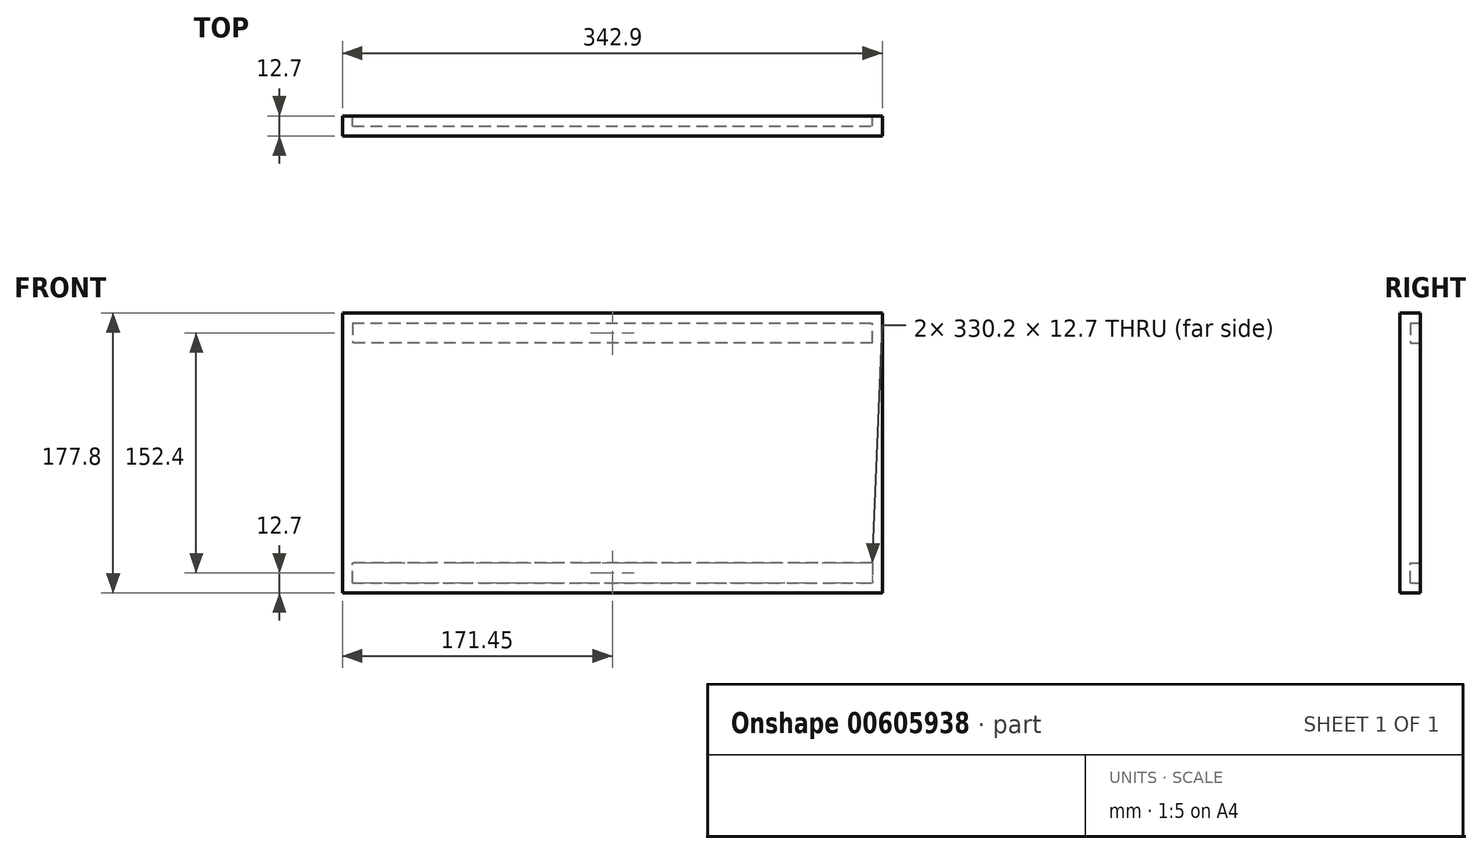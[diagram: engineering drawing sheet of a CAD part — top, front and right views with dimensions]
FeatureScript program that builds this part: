
annotation { "Feature Type Name" : "Feature", "Feature Type Description" : "" }
export const myFeature = defineFeature(function(context is Context, id is Id, definition is map)
    precondition{}
    {
        {
            var Q0;
            Q0=qCreatedBy(makeId("Front.planeOp"),FACE);
            var sketch = newSketch(context, id + "F0", { "sketchPlane" : qUnion([Q0])});
            skLineSegment(sketch, "E0.bottom", {"start": v(0, 0) * mm, "end": v(342.9, 0) * mm});
            skLineSegment(sketch, "E0.top", {"start": v(0, 177.8) * mm, "end": v(342.9, 177.8) * mm});
            skLineSegment(sketch, "E0.left", {"start": v(0, 0) * mm, "end": v(0, 177.8) * mm});
            skLineSegment(sketch, "E0.right", {"start": v(342.9, 0) * mm, "end": v(342.9, 177.8) * mm});
            skSolve(sketch);
        }
        {
            var Q0;
            Q0=makeQuery(id+"F0.imprint","IMPRINT",FACE,{"disambiguationData":[TD([[makeQuery(id+"F0.imprint","IMPRINT",EDGE,{"derivedFrom":sQuery(id+"F0.wireOp",EDGE,"E0.bottom")}),1.0]])]});
            extrude(context, id + "F1", {"entities" : qUnion([Q0]), "depth" : 12.7 * mm, "offsetDistance" : 25.4 * mm});
        }
        {
            var Q0;
            Q0=makeQuery(id+"F1.opExtrude","CAP_FACE",FACE,{"disambiguationData":[OSD([sQuery(id+"F0.wireOp",EDGE,"E0.bottom"),sQuery(id+"F0.wireOp",EDGE,"E0.top"),sQuery(id+"F0.wireOp",EDGE,"E0.left"),sQuery(id+"F0.wireOp",EDGE,"E0.right")])],"isStart":true});
            var sketch = newSketch(context, id + "F2", { "sketchPlane" : qUnion([Q0])});
            skLineSegment(sketch, "E1", {"start": v(-342.9, 0) * mm, "end": v(-342.9, 6.35) * mm});
            skLineSegment(sketch, "E2", {"start": v(-342.9, 6.35) * mm, "end": v(-342.9, 19.05) * mm});
            skLineSegment(sketch, "E3", {"start": v(-342.9, 19.05) * mm, "end": v(0, 19.05) * mm});
            skLineSegment(sketch, "E4", {"start": v(0, 19.05) * mm, "end": v(0, 6.35) * mm});
            skLineSegment(sketch, "E5", {"start": v(0, 6.35) * mm, "end": v(-342.9, 6.35) * mm});
            skLineSegment(sketch, "E6", {"start": v(-342.9, 19.05) * mm, "end": v(-336.55, 19.05) * mm});
            skLineSegment(sketch, "E7", {"start": v(-336.55, 19.05) * mm, "end": v(-336.55, 6.35) * mm});
            skLineSegment(sketch, "E8", {"start": v(-336.55, 6.35) * mm, "end": v(0, 6.35) * mm});
            skLineSegment(sketch, "E9", {"start": v(0, 6.35) * mm, "end": v(-6.35, 6.35) * mm});
            skLineSegment(sketch, "E10", {"start": v(-6.35, 6.35) * mm, "end": v(-6.35, 19.05) * mm});
            skSolve(sketch);
        }
        {
            var Q0;
            {var subQ0=sQuery(id+"F2.wireOp",EDGE,"E7");Q0=makeQuery(id+"F2.imprint","IMPRINT",FACE,{"disambiguationData":[TD([[makeQuery(id+"F2.imprint","IMPRINT",EDGE,{"derivedFrom":subQ0}),1.0]])]});}
            extrude(context, id + "F3", {"entities" : qUnion([Q0]), "operationType" : NewBodyOperationType.REMOVE, "oppositeDirection" : true, "depth" : 6.35 * mm, "offsetDistance" : 25.4 * mm});
        }
        {
            var Q0;
            Q0=makeQuery(id+"F1.opExtrude","CAP_FACE",FACE,{"disambiguationData":[OSD([sQuery(id+"F0.wireOp",EDGE,"E0.bottom"),sQuery(id+"F0.wireOp",EDGE,"E0.top"),sQuery(id+"F0.wireOp",EDGE,"E0.left"),sQuery(id+"F0.wireOp",EDGE,"E0.right")])],"isStart":true});
            var sketch = newSketch(context, id + "F4", { "sketchPlane" : qUnion([Q0])});
            skLineSegment(sketch, "E11", {"start": v(-342.9, 177.8) * mm, "end": v(-342.9, 171.45) * mm});
            skLineSegment(sketch, "E12", {"start": v(-342.9, 171.45) * mm, "end": v(-342.9, 158.75) * mm});
            skLineSegment(sketch, "E13", {"start": v(-342.9, 158.75) * mm, "end": v(0, 158.75) * mm});
            skLineSegment(sketch, "E14", {"start": v(0, 158.75) * mm, "end": v(0, 171.45) * mm});
            skLineSegment(sketch, "E15", {"start": v(0, 171.45) * mm, "end": v(-342.9, 171.45) * mm});
            skLineSegment(sketch, "E16", {"start": v(-342.9, 158.75) * mm, "end": v(-336.55, 158.75) * mm});
            skLineSegment(sketch, "E17", {"start": v(-336.55, 158.75) * mm, "end": v(-336.55, 171.45) * mm});
            skLineSegment(sketch, "E18", {"start": v(-336.55, 171.45) * mm, "end": v(0, 171.45) * mm});
            skLineSegment(sketch, "E19", {"start": v(-6.35, 171.45) * mm, "end": v(0, 171.45) * mm});
            skLineSegment(sketch, "E20", {"start": v(-6.35, 171.45) * mm, "end": v(-6.35, 158.75) * mm});
            skSolve(sketch);
        }
        {
            var Q0;
            {var subQ0=sQuery(id+"F4.wireOp",EDGE,"E17");Q0=makeQuery(id+"F4.imprint","IMPRINT",FACE,{"disambiguationData":[TD([[makeQuery(id+"F4.imprint","IMPRINT",EDGE,{"derivedFrom":subQ0}),-1.0]])]});}
            extrude(context, id + "F5", {"entities" : qUnion([Q0]), "operationType" : NewBodyOperationType.REMOVE, "oppositeDirection" : true, "depth" : 6.35 * mm, "offsetDistance" : 25.4 * mm});
        }
    });
